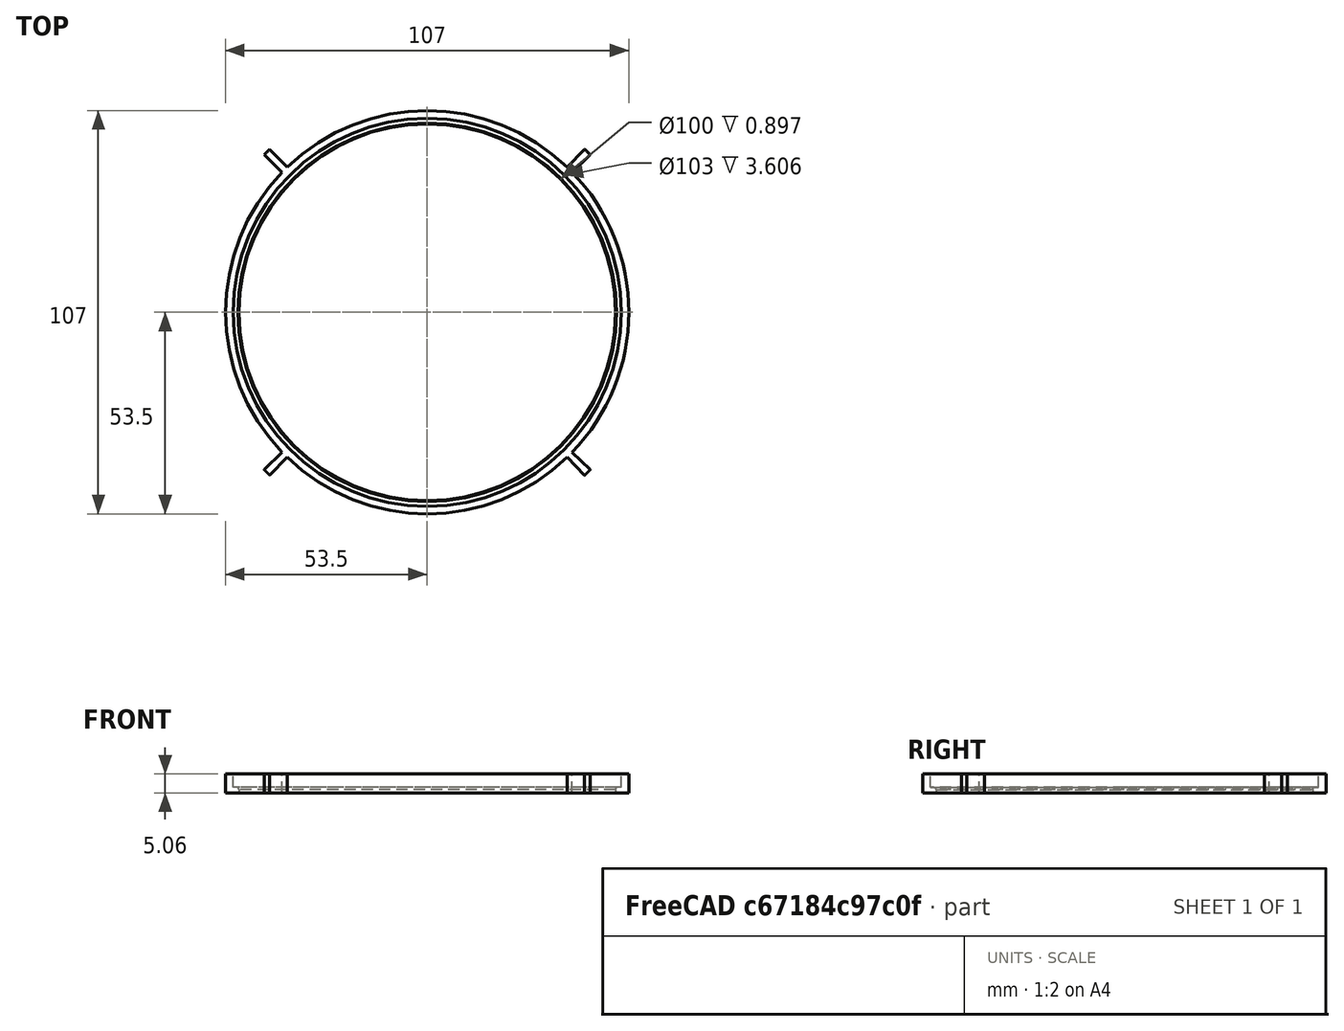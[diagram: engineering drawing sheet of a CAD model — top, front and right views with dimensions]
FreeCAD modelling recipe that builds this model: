
FCSTD DOCUMENT  (FreeCAD 0.18.4R)
Label: 15
License: All rights reserved
LicenseURL: http://en.wikipedia.org/wiki/All_rights_reserved
objects: Sketcher::SketchObject×5, PartDesign::Revolution×2, PartDesign::Plane×2, PartDesign::Pad×1, PartDesign::MultiTransform×1, PartDesign::Mirrored×1, PartDesign::PolarPattern×1, PartDesign::Pocket×1, PartDesign::Body×1
note: 19 computed .brp shape members not serialized (recipe doc carries the construction recipe); baked Part::Feature solids carry a one-line shape summary decoded from their .brp

FEATURE [Sketcher::SketchObject] Sketch  label="Sketch001"
  MapMode = 5
  Support = -> [XY_Plane]
  constraints (23):
    c: Vertical(g0)
    c: Coincident(g1,g0)
    c: Coincident(g2,g1)
    c: Horizontal(g2)
    c: Coincident(g3,g2)
    c: Vertical(g3)
    c: Distance(g0,g-2) = 50
    c: Distance(g2,g-2) = 51.5
    c: PointOnObject(g0,g-1)
    c: Distance(g0) = 20
    c: Distance(g3) = 50
    c: Angle(g0,g1) = 2.79253
    c: DistanceX(g0,g1) = 0.2
    c: Coincident(g4,g3)
    c: Coincident(g4,g5)
    c: Horizontal(g5)
    c: Coincident(g5,g6)
    c: PointOnObject(g6,g-1)
    c: Vertical(g6)
    c: Coincident(g6,g7)
    c: Coincident(g7,g0)
    c: Distance(g5) = 0.8
    c: Distance(g3,g6) = 2
FEATURE [PartDesign::Revolution] Revolution  label="Unnamed"
  Angle = 360
  Axis = (0,1,0)
  Base = (0,0,0)
FEATURE [Sketcher::SketchObject] Sketch001  label="Unnamed"
FEATURE [PartDesign::Pad] Pad
  BaseFeature = -> Revolution
  Length = 2
  Length2 = 100
  Placement = pos=(0,0,0) rot=(1,0,0;1.5708rad)
  Profile = -> Sketch001
  Reversed = true
  Type = 0
FEATURE [PartDesign::Revolution] Revolution001  label="Unnamed"
  Angle = 360
  Axis = (0,1,0)
  Base = (0,0,0)
FEATURE [PartDesign::MultiTransform] MultiTransform  label="Unnamed"
FEATURE [PartDesign::Mirrored] Mirrored  label="Unnamed"
FEATURE [PartDesign::PolarPattern] PolarPattern  label="Unnamed"
  Angle = 360
  Occurrences = 3
FEATURE [PartDesign::Plane] DatumPlane  label="Unnamed"
  Length = 24
  ResizeMode = 0
  Width = 24
FEATURE [Sketcher::SketchObject] Sketch002  label="Sketch003"
  ExternalGeometry = -> [Pad]
  MapMode = 5
  Placement = pos=(53.5,1.138e-13,73.197) rot=(0,1,0;1.5708rad)
  Support = -> [DatumPlane]
  constraints (10):
    c: Coincident(g0,g-4)
    c: Horizontal(g0)
    c: PointOnObject(g1,g-2)
    c: Coincident(g1,g0)
    c: Distance(g-3,g1) = 3
    c: Coincident(g2,g0)
    c: Vertical(g2)
    c: Coincident(g3,g2)
    c: Coincident(g3,g1)
    c: Horizontal(g3)
FEATURE [Sketcher::SketchObject] Sketch003  label="Unnamed"
FEATURE [PartDesign::Plane] DatumPlane001
  Length = 24
  MapMode = 5
  Placement = pos=(0,3.19e-14,20.5495) rot=(0,0,1;3.14159rad)
  ResizeMode = 0
  Support = -> [MultiTransform]
  Width = 24
FEATURE [Sketcher::SketchObject] Sketch004  label="Unnamed"
  constraints (26):
    c: Coincident(g0,g1)
    c: Coincident(g1,g2)
    c: Coincident(g2,g3)
    c: Coincident(g3,g0)
    c: Horizontal(g0)
    c: Horizontal(g2)
    c: Vertical(g1)
    c: Vertical(g3)
    c: Coincident(g4,g5)
    c: Coincident(g5,g6)
    c: Coincident(g6,g7)
    c: Coincident(g7,g4)
    c: Horizontal(g4)
    c: Horizontal(g6)
    c: Vertical(g5)
    c: Vertical(g7)
    c: Coincident(g4,g0)
    c: Coincident(g8,g9)
    c: Coincident(g9,g10)
    c: Coincident(g10,g11)
    c: Coincident(g11,g8)
    c: Horizontal(g8)
    c: Horizontal(g10)
    c: Vertical(g9)
    c: Vertical(g11)
    c: Coincident(g8,g1)
FEATURE [PartDesign::Pocket] Pocket  label="Unnamed"
  Length = 100
  Length2 = 100
  Type = 0
FEATURE [PartDesign::Body] Body
  Group = -> [Sketch,Revolution,Sketch001,Pad,Sketch002,Revolution001,MultiTransform,Mirrored,PolarPattern,DatumPlane,Sketch003,DatumPlane001,Sketch004,Pocket]
  Origin = -> Origin
  Tip = -> Pocket
